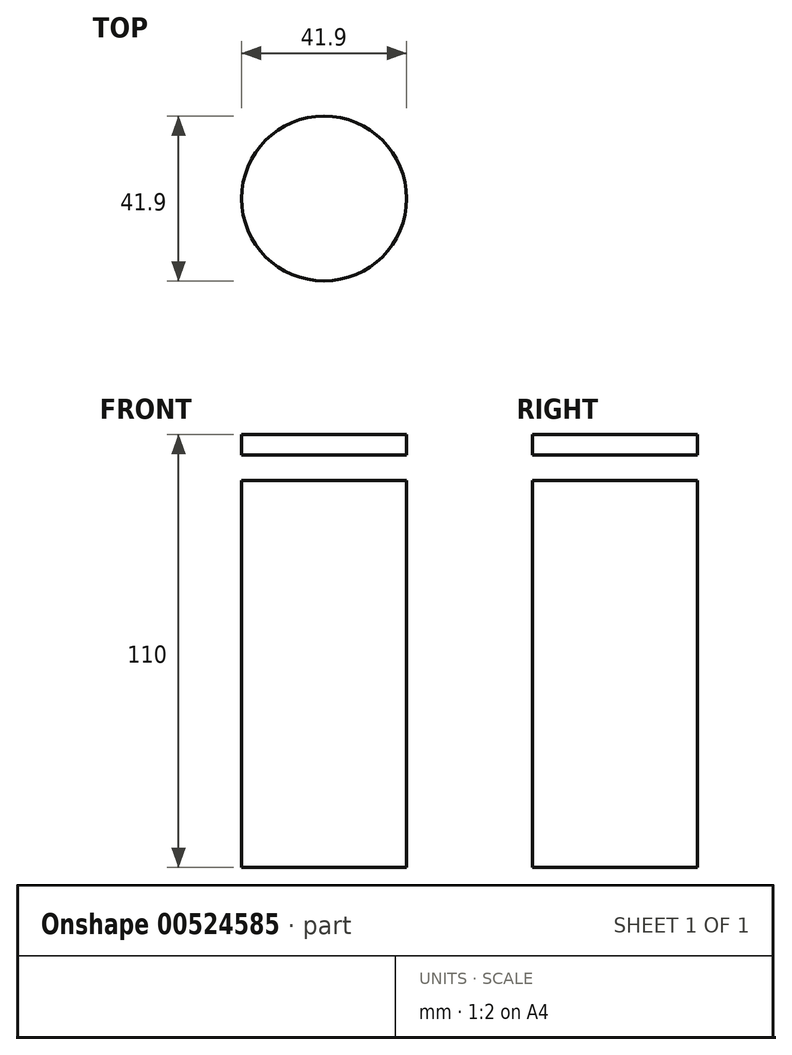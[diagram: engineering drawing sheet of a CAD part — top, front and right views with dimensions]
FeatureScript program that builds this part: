
annotation { "Feature Type Name" : "Feature", "Feature Type Description" : "" }
export const myFeature = defineFeature(function(context is Context, id is Id, definition is map)
    precondition{}
    {
        {
            var Q0;
            Q0=qCreatedBy(makeId("Top.planeOp"),FACE);
            cPlane(context, id + "F0", {"entities" : qUnion([Q0]), "cplaneType" : CPlaneType.OFFSET, "offset" : 88.3 * mm, "oppositeDirection" : true, "width" : 150 * mm, "height" : 150 * mm});
        }
        {
            var Q0;
            Q0=qCreatedBy(id+"F0.planeOp",FACE);
            var sketch = newSketch(context, id + "F1", { "sketchPlane" : qUnion([Q0])});
            skCircle(sketch, "E0", {"center": v(0, 0) * mm, "radius": 20.95 * mm});
            skSolve(sketch);
        }
        {
            var Q0;
            Q0 = qSketchRegion(id + "F1", true);
            extrude(context, id + "F2", {"entities" : qUnion([Q0]), "depth" : 110 * mm, "offsetDistance" : 25 * mm});
        }
        {
            var Q0;
            Q0=qCreatedBy(makeId("Top.planeOp"),FACE);
            cPlane(context, id + "F3", {"entities" : qUnion([Q0]), "cplaneType" : CPlaneType.OFFSET, "offset" : 10 * mm, "width" : 150 * mm, "height" : 150 * mm});
        }
        {
            var Q0;
            Q0=qCreatedBy(makeId("Top.planeOp"),FACE);
            cPlane(context, id + "F4", {"entities" : qUnion([Q0]), "cplaneType" : CPlaneType.OFFSET, "offset" : 10 * mm, "oppositeDirection" : true, "width" : 150 * mm, "height" : 150 * mm});
        }
        {
            var Q0;
            Q0=qCreatedBy(id+"F4.planeOp",FACE);
            cPlane(context, id + "F5", {"entities" : qUnion([Q0]), "cplaneType" : CPlaneType.OFFSET, "offset" : 10 * mm, "oppositeDirection" : true, "width" : 150 * mm, "height" : 150 * mm});
        }
        {
            var Q0;
            Q0=qCreatedBy(id+"F5.planeOp",FACE);
            cPlane(context, id + "F6", {"entities" : qUnion([Q0]), "cplaneType" : CPlaneType.OFFSET, "offset" : 10 * mm, "oppositeDirection" : true, "width" : 150 * mm, "height" : 150 * mm});
        }
        {
            var Q0;
            Q0=qCreatedBy(id+"F3.planeOp",FACE);
            var sketch = newSketch(context, id + "F7", { "sketchPlane" : qUnion([Q0])});
            skCircle(sketch, "E1", {"center": v(0, 0) * mm, "radius": 22.5 * mm});
            skSolve(sketch);
        }
        {
            var Q0;
            Q0 = qSketchRegion(id + "F7", true);
            extrude(context, id + "F8", {"entities" : qUnion([Q0]), "operationType" : NewBodyOperationType.REMOVE, "depth" : 6.5 * mm, "offsetDistance" : 25 * mm});
        }
    });
